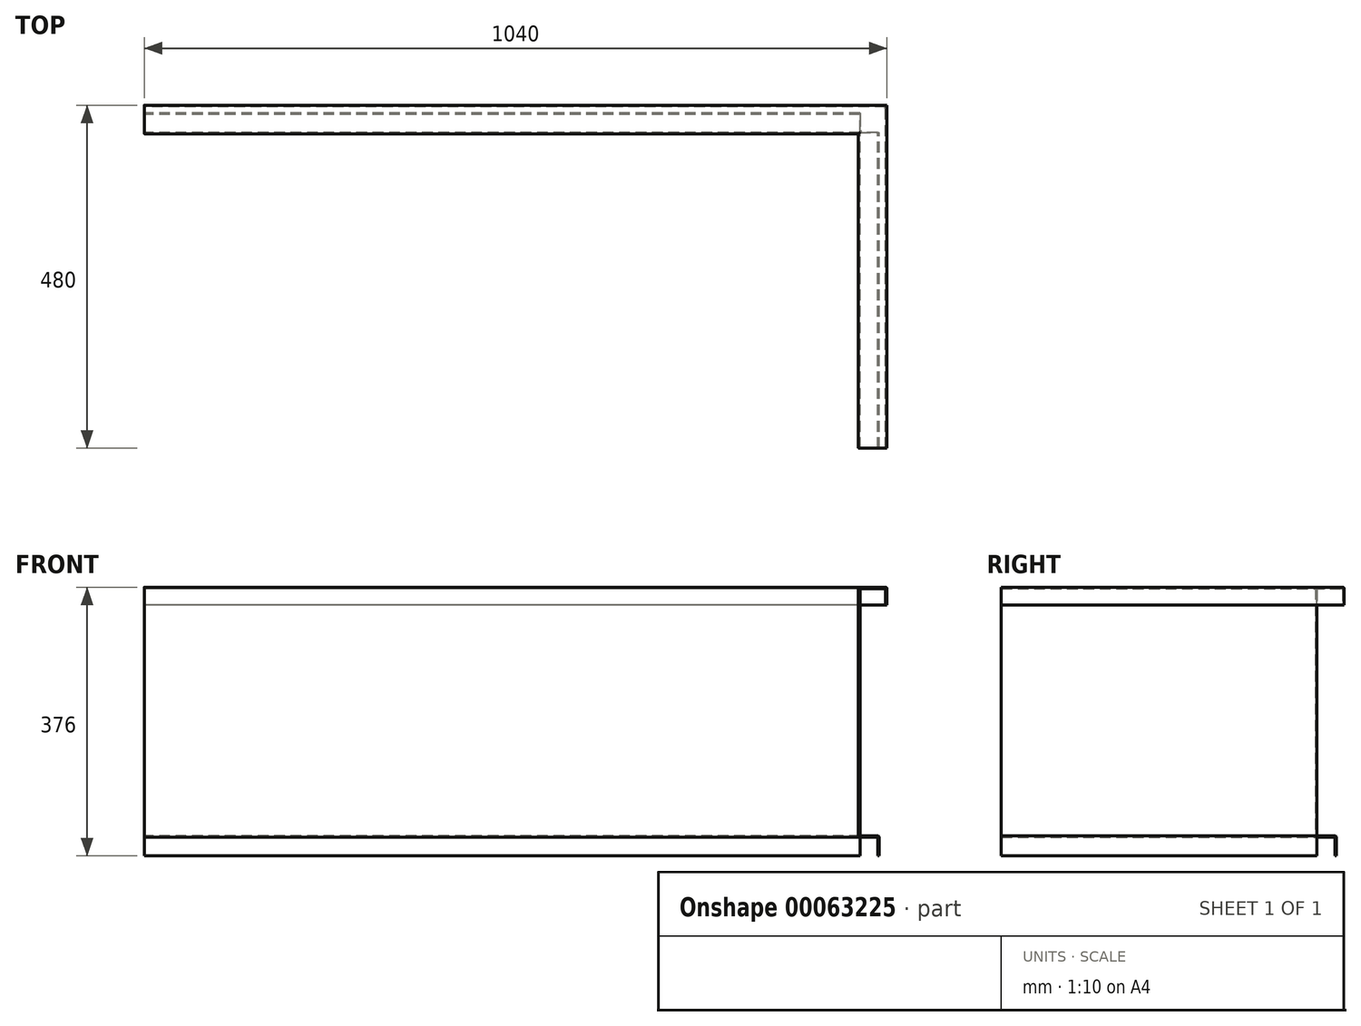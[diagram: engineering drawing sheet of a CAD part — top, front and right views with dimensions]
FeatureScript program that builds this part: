
annotation { "Feature Type Name" : "Feature", "Feature Type Description" : "" }
export const myFeature = defineFeature(function(context is Context, id is Id, definition is map)
    precondition{}
    {
        {
            var Q0;
            Q0=qCreatedBy(makeId("Front.planeOp"),FACE);
            var sketch = newSketch(context, id + "F0", { "sketchPlane" : qUnion([Q0])});
            skLineSegment(sketch, "E0", {"start": v(38, -25) * mm, "end": v(38, -2) * mm});
            skLineSegment(sketch, "E1", {"start": v(38, -2) * mm, "end": v(2, -2) * mm});
            skLineSegment(sketch, "E2", {"start": v(2, -2) * mm, "end": v(2, -348) * mm});
            skLineSegment(sketch, "E3", {"start": v(2, -348) * mm, "end": v(29, -348) * mm});
            skLineSegment(sketch, "E4", {"start": v(29, -348) * mm, "end": v(29, -376) * mm});
            skLineSegment(sketch, "E5.0", {"start": v(27, -350) * mm, "end": v(27, -376) * mm});
            skLineSegment(sketch, "E5.1", {"start": v(40, -25) * mm, "end": v(40, 0) * mm});
            skLineSegment(sketch, "E5.2", {"start": v(40, 0) * mm, "end": v(0, 0) * mm});
            skLineSegment(sketch, "E5.3", {"start": v(0, 0) * mm, "end": v(0, -350) * mm});
            skLineSegment(sketch, "E5.4", {"start": v(0, -350) * mm, "end": v(27, -350) * mm});
            skLineSegment(sketch, "E6", {"start": v(27, -376) * mm, "end": v(29, -376) * mm});
            skLineSegment(sketch, "E7", {"start": v(38, -25) * mm, "end": v(40, -25) * mm});
            skSolve(sketch);
        }
        {
            var Q0;
            Q0=qCreatedBy(makeId("Top.planeOp"),FACE);
            var sketch = newSketch(context, id + "F1", { "sketchPlane" : qUnion([Q0])});
            skLineSegment(sketch, "E8", {"start": v(0, 0) * mm, "end": v(0, 440) * mm});
            skLineSegment(sketch, "E9", {"start": v(0, 440) * mm, "end": v(-1000, 440) * mm});
            skSolve(sketch);
        }
        {
            var Q0;
            Q0=qSketchRegion(id+"F0",true);
            var Q1;
            Q1=qConstructionFilter(qBodyType(qCreatedBy(id+"F1",EDGE),BodyType.WIRE),ConstructionObject.NO);
            sweep(context, id + "F2", {"profiles" : qUnion([Q0]), "path" : qUnion([Q1])});
        }
        {
            var Q0;
            Q0=makeQuery(id+"F2.opSweep","SWEPT_FACE",FACE,{"disambiguationData":[OSD([sQuery(id+"F0.wireOp",EDGE,"E3"),sQuery(id+"F1.wireOp",EDGE,"E8")])]});
            var sketch = newSketch(context, id + "F3", { "sketchPlane" : qUnion([Q0])});
            skLineSegment(sketch, "E10", {"start": v(2, 442) * mm, "end": v(2, 469) * mm});
            skLineSegment(sketch, "E11", {"start": v(2, 469) * mm, "end": v(29, 469) * mm});
            skLineSegment(sketch, "E12", {"start": v(29, 469) * mm, "end": v(29, 442) * mm});
            skLineSegment(sketch, "E13", {"start": v(29, 442) * mm, "end": v(2, 442) * mm});
            skSolve(sketch);
        }
        {
            var Q0;
            Q0=qSketchRegion(id+"F3",true);
            extrude(context, id + "F4", {"entities" : qUnion([Q0]), "operationType" : NewBodyOperationType.REMOVE, "oppositeDirection" : true, "depth" : 30 * mm});
        }
        {
            var Q0;
            Q0=makeQuery(id+"F2.opSweep","SWEPT_EDGE",EDGE,{"disambiguationData":[OSD([sQuery(id+"F0.wireOp",EDGE,"E3"),sQuery(id+"F0.wireOp",EDGE,"E4"),sQuery(id+"F1.wireOp",EDGE,"E9")])]});
            var Q1;
            Q1=makeQuery(id+"F2.opSweep","SWEPT_EDGE",EDGE,{"disambiguationData":[OSD([sQuery(id+"F0.wireOp",EDGE,"E2"),sQuery(id+"F0.wireOp",EDGE,"E3"),sQuery(id+"F1.wireOp",EDGE,"E9")])]});
            var Q2;
            Q2=makeQuery(id+"F2.opSweep","SWEPT_EDGE",EDGE,{"disambiguationData":[OSD([sQuery(id+"F0.wireOp",EDGE,"E5.1"),sQuery(id+"F0.wireOp",EDGE,"E5.2"),sQuery(id+"F1.wireOp",EDGE,"E9")])]});
            var Q3;
            Q3=makeQuery(id+"F2.opSweep","SWEPT_EDGE",EDGE,{"disambiguationData":[OSD([sQuery(id+"F0.wireOp",EDGE,"E5.2"),sQuery(id+"F0.wireOp",EDGE,"E5.3"),sQuery(id+"F1.wireOp",EDGE,"E9")])]});
            var Q4;
            Q4=makeQuery(id+"F2.opSweep","SWEPT_EDGE",EDGE,{"disambiguationData":[OSD([sQuery(id+"F0.wireOp",EDGE,"E5.2"),sQuery(id+"F0.wireOp",EDGE,"E5.3"),sQuery(id+"F1.wireOp",EDGE,"E8")])]});
            var Q5;
            Q5=makeQuery(id+"F2.opSweep","SWEPT_EDGE",EDGE,{"disambiguationData":[OSD([sQuery(id+"F0.wireOp",EDGE,"E5.1"),sQuery(id+"F0.wireOp",EDGE,"E5.2"),sQuery(id+"F1.wireOp",EDGE,"E8")])]});
            var Q6;
            Q6=makeQuery(id+"F2.opSweep","SWEPT_EDGE",EDGE,{"disambiguationData":[OSD([sQuery(id+"F0.wireOp",EDGE,"E3"),sQuery(id+"F0.wireOp",EDGE,"E4"),sQuery(id+"F1.wireOp",EDGE,"E8")])]});
            var Q7;
            Q7=makeQuery(id+"F2.opSweep","SWEPT_EDGE",EDGE,{"disambiguationData":[OSD([sQuery(id+"F0.wireOp",EDGE,"E5.3"),sQuery(id+"F0.wireOp",EDGE,"E5.4"),sQuery(id+"F1.wireOp",EDGE,"E8")])]});
            var Q8;
            Q8=makeQuery(id+"F2.opSweep","SWEPT_EDGE",EDGE,{"disambiguationData":[OSD([sQuery(id+"F0.wireOp",EDGE,"E5.3"),sQuery(id+"F0.wireOp",EDGE,"E5.4"),sQuery(id+"F1.wireOp",EDGE,"E9")])]});
            var Q9;
            Q9=makeQuery(id+"F2.opSweep","SWEPT_EDGE",EDGE,{"disambiguationData":[OSD([sQuery(id+"F0.wireOp",EDGE,"E5.0"),sQuery(id+"F0.wireOp",EDGE,"E5.4"),sQuery(id+"F1.wireOp",EDGE,"E9")])]});
            var Q10;
            Q10=makeQuery(id+"F2.opSweep","SWEPT_EDGE",EDGE,{"disambiguationData":[OSD([sQuery(id+"F0.wireOp",EDGE,"E0"),sQuery(id+"F0.wireOp",EDGE,"E1"),sQuery(id+"F1.wireOp",EDGE,"E9")])]});
            var Q11;
            Q11=makeQuery(id+"F2.opSweep","SWEPT_EDGE",EDGE,{"disambiguationData":[OSD([sQuery(id+"F0.wireOp",EDGE,"E1"),sQuery(id+"F0.wireOp",EDGE,"E2"),sQuery(id+"F1.wireOp",EDGE,"E9")])]});
            var Q12;
            Q12=makeQuery(id+"F2.opSweep","SWEPT_EDGE",EDGE,{"disambiguationData":[OSD([sQuery(id+"F0.wireOp",EDGE,"E5.0"),sQuery(id+"F0.wireOp",EDGE,"E5.4"),sQuery(id+"F1.wireOp",EDGE,"E8")])]});
            var Q13;
            Q13=makeQuery(id+"F2.opSweep","SWEPT_EDGE",EDGE,{"disambiguationData":[OSD([sQuery(id+"F0.wireOp",EDGE,"E0"),sQuery(id+"F0.wireOp",EDGE,"E1"),sQuery(id+"F1.wireOp",EDGE,"E8")])]});
            var Q14;
            Q14=makeQuery(id+"F2.opSweep","SWEPT_EDGE",EDGE,{"disambiguationData":[OSD([sQuery(id+"F0.wireOp",EDGE,"E1"),sQuery(id+"F0.wireOp",EDGE,"E2"),sQuery(id+"F1.wireOp",EDGE,"E8")])]});
            fillet(context, id + "F5", {"entities" : qUnion([Q0, Q1, Q2, Q3, Q4, Q5, Q6, Q7, Q8, Q9, Q10, Q11, Q12, Q13, Q14]), "radius" : 2 * mm, "tangentPropagation" : true, "allowEdgeOverflow" : false});
        }
    });
